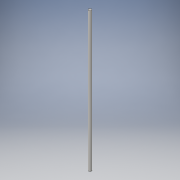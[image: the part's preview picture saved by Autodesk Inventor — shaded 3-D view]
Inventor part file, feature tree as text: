
AUTODESK INVENTOR PART (.ipt)
format: ipt  version: 2016 (Build 200138000, 138)  size: 84,992 bytes
history: native  units: in
note: dims shown in document units (in); Inventor stores cm internally (conversion verified against a paired STEP export)
features: extrude x1, sketch x1
ambient origin geometry x8: Origin, YZ Plane, XZ Plane, XY Plane, X Axis, Y Axis, Z Axis, Center Point
bodies: Solid1 (feature_tree)
feature tree (2):
  extrude  "Extrusion1"  Depth=12.0in
  sketch  "Sketch1"  dims[d0=12.0in d1=0.0in d2=0.25in]
